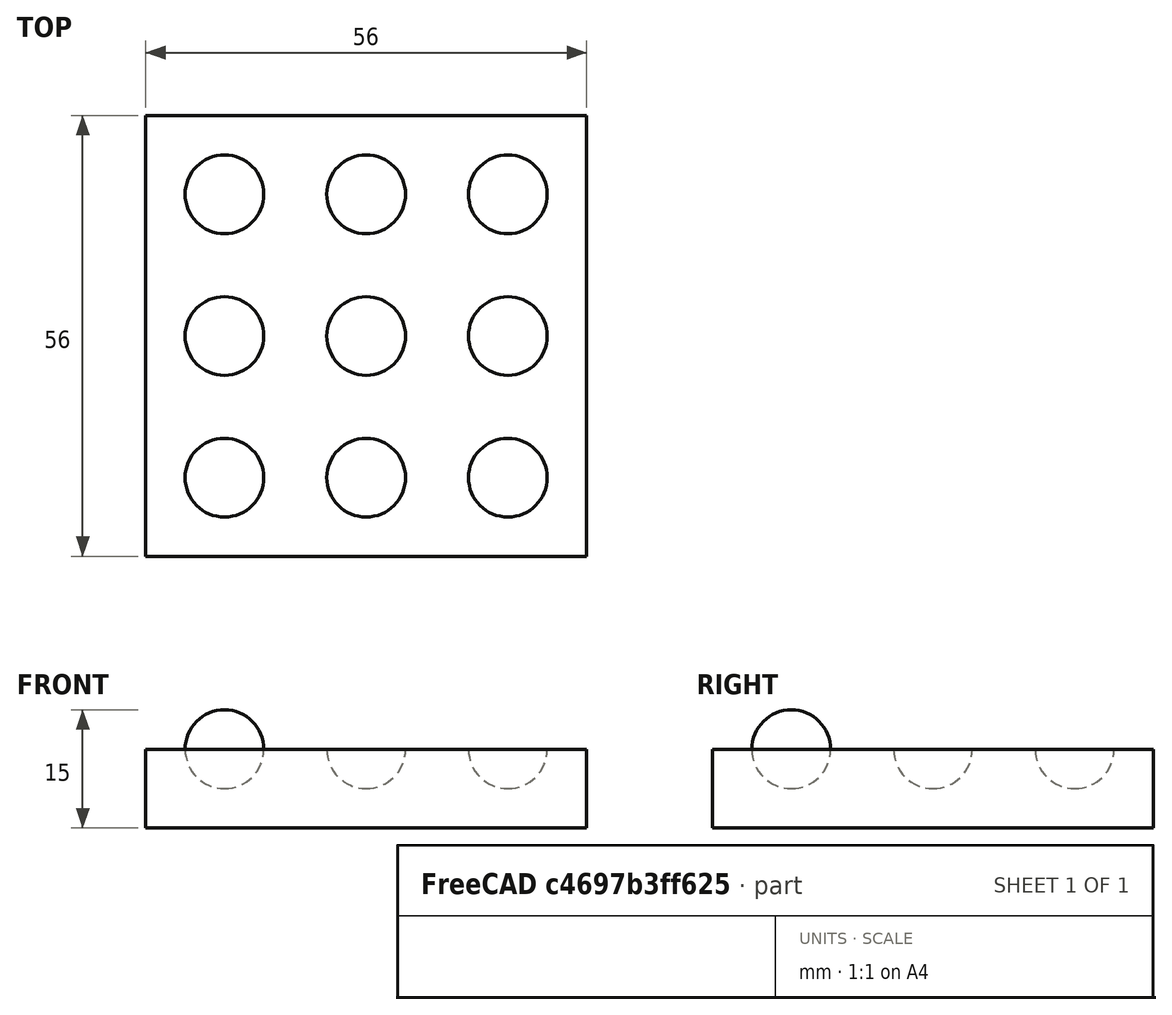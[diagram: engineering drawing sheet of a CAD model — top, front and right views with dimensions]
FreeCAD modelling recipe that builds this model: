
FCSTD DOCUMENT  (FreeCAD 1.0R39319 (Git))
Label: ojt1_t13p01_spheres
License: All rights reserved
LicenseURL: https://en.wikipedia.org/wiki/All_rights_reserved
objects: Part::Sphere×1, Part::FeaturePython×1, Part::Box×1, Part::Cut×1
note: 3 computed .brp shape members not serialized (recipe doc carries the construction recipe); baked Part::Feature solids carry a one-line shape summary decoded from their .brp

FEATURE [Part::Sphere] Sphere
  Angle1 = -90
  Angle2 = 90
  Angle3 = 360
  AttacherType = Attacher::AttachEngine3D
  Radius = 5
FEATURE [Part::FeaturePython] Array  # Draft array (typed FeaturePython)
  AlwaysSyncPlacement = false
  Angle = 360
  ArrayType = 0
  Axis = (0,0,1)
  Base = -> Sphere
  Center = (0,0,0)
  Count = 9
  ExpandArray = false
  Fuse = false
  IntervalAxis = (0,0,0)
  IntervalX = (18,0,0)
  IntervalY = (0,18,0)
  IntervalZ = (0,0,100)
  NumberCircles = 3
  NumberPolar = 5
  NumberX = 3
  NumberY = 3
  NumberZ = 1
  PlacementList = 9 placements: [(0,0,0),(0,18,0),(0,36,0),(18,0,0),(18,18,0),(18,36,0),(36,0,0),(36,18,0),(36,36,0)]
  RadialDistance = 50
  ScaleList = (9) [(1,1,1),(1,1,1),(1,1,1),(1,1,1),(1,1,1),(1,1,1),(1,1,1),(1,1,1),(1,1,1)]
  Symmetry = 1
  TangentialDistance = 25
FEATURE [Part::Box] Box  label="Cube"
  AttacherType = Attacher::AttachEngine3D
  Height = 10
  Length = 56
  Placement = pos=(-10,-10,-10) rot=(0,0,1;0rad)
  Width = 56
FEATURE [Part::Cut] Cut
  Base = -> Box
  Refine = true
  Tool = -> Array
